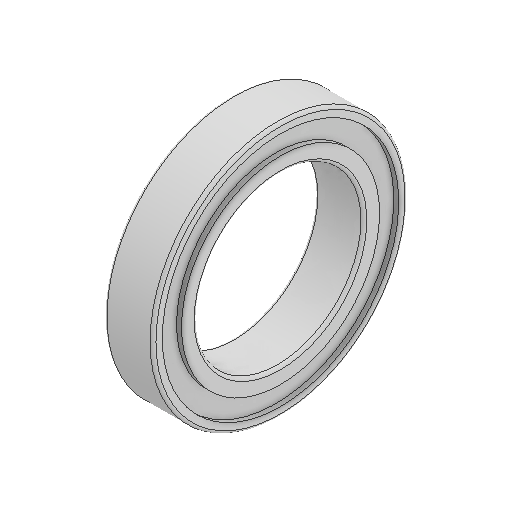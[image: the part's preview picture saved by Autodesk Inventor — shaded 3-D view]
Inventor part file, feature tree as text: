
AUTODESK INVENTOR PART (.ipt)
format: ipt  version: 2024.1 (Build 281209000, 209)  size: 166,400 bytes
history: native  units: in
note: dims shown in document units (in); Inventor stores cm internally (conversion verified against a paired STEP export)
features: fillet x1
ambient origin geometry x8: Origin, YZ Plane, XZ Plane, XY Plane, X Axis, Y Axis, Z Axis, Center Point
bodies: Solid1 (feature_tree)
feature tree (1):
  fillet  "Fillet1"  [1 undecoded]
note: 1 required parameter value undecoded (feature->parameter linkage not recoverable at this tier; creation-order binding heuristic only, values carry confidence <= 0.55)
